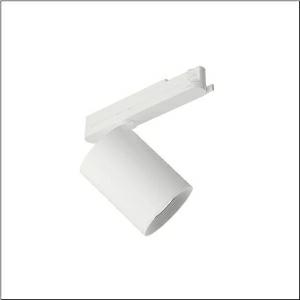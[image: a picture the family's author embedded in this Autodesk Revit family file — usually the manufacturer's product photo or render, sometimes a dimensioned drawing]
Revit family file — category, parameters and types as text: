
# Revit family: spot_21_51se12mbd5b
name_source: partatom
category: Lighting Fixtures
units: mm (PartAtom-declared; Revit-internal decimal feet)

## family parameters
Cut with Voids When Loaded = No
Host = Face
Light Source = No
Part Type = Normal
Room Calculation Point = No
Round Connector Dimension = Use Diameter
Shared = No

## types (1)
- --- (1 x LED, 5460 lm, 41.5 W, 4000K)
    Apparent Load = 42 VA
    CIE Flux Codes = 95 98 99 100 100
    Color Rendering = 90
    Color Temperature = 4000K
    Default Elevation = 1800 mm
    Description = Spot 21, directional spotlight, light control with lens, of PMMA, LED rated luminous flux: 5.250lm, light colour: 940, control gear: ECG Multilumen, with 3-phase adapter, mains connection: 220..240V, AC, 50/60Hz, of aluminium, traffic white (RAL 9016), length: 213mm, diameter: 105mm, protection rating (complete): IP20, insulation class (complete): insulation class I (protective earthing), certification: CE, impact resistance: IK02, permissible ambient temperature for indoor applications: -20..+40°C, packaging unit: 1 piece
    Height = 175 mm
    Lamp = 1 x LED
    Lamp Light Flux = 5460 lm
    Lamp Power = 41.5 W
    Lamp count = 1
    Length = 105 mm
    Luminous efficacy = 132 lm/W
    Manufacturer = Siteco
    ModVariant = No
    Model = 51SE12MBD5B
    Mounting Place = Ceiling
    Mounting Type = Pendant
    Number of Poles = 1
    OnlyDefault = Yes
    Power Factor = 1
    Product Name = Spot 21
    Product group = directional spotlight
    ProductGroupID = 905
    Protection Class = Protection class I
    Protection Degree = IP 20
    RLX_Detail_Level = 1
    RLX_Emergency_Light_Flux = 0 lm
    RLX_Emergency_Type = 0
    RLX_Emergency_Type_DB = No
    RlxData = <blob elided: 17637 chars, md5=5aa50e6d>
    Socket = socket
    Standby Power = 0 W
    System Light Flux = 5460 lm
    System Power = 42 W
    Type Comments = factory setting: luminous flux: 100 % | (ON | ON | ON | ON) | 1050 mA
    Type Image = l_1003976.jpg
    URL = http://relux.com
    VarID = @adj_165953
    Voltage = 0 V
    Weight = 0.00 kg
    Width = 0 mm  [stored 0 ft]

note: [stored X ft] marks values corroborated as IEEE doubles in the binary element streams (Revit-internal decimal feet)

## geometry (parser evidence)
native form markers: Blend x4, Sweep x10
no freeform markers — native parametric forms only
